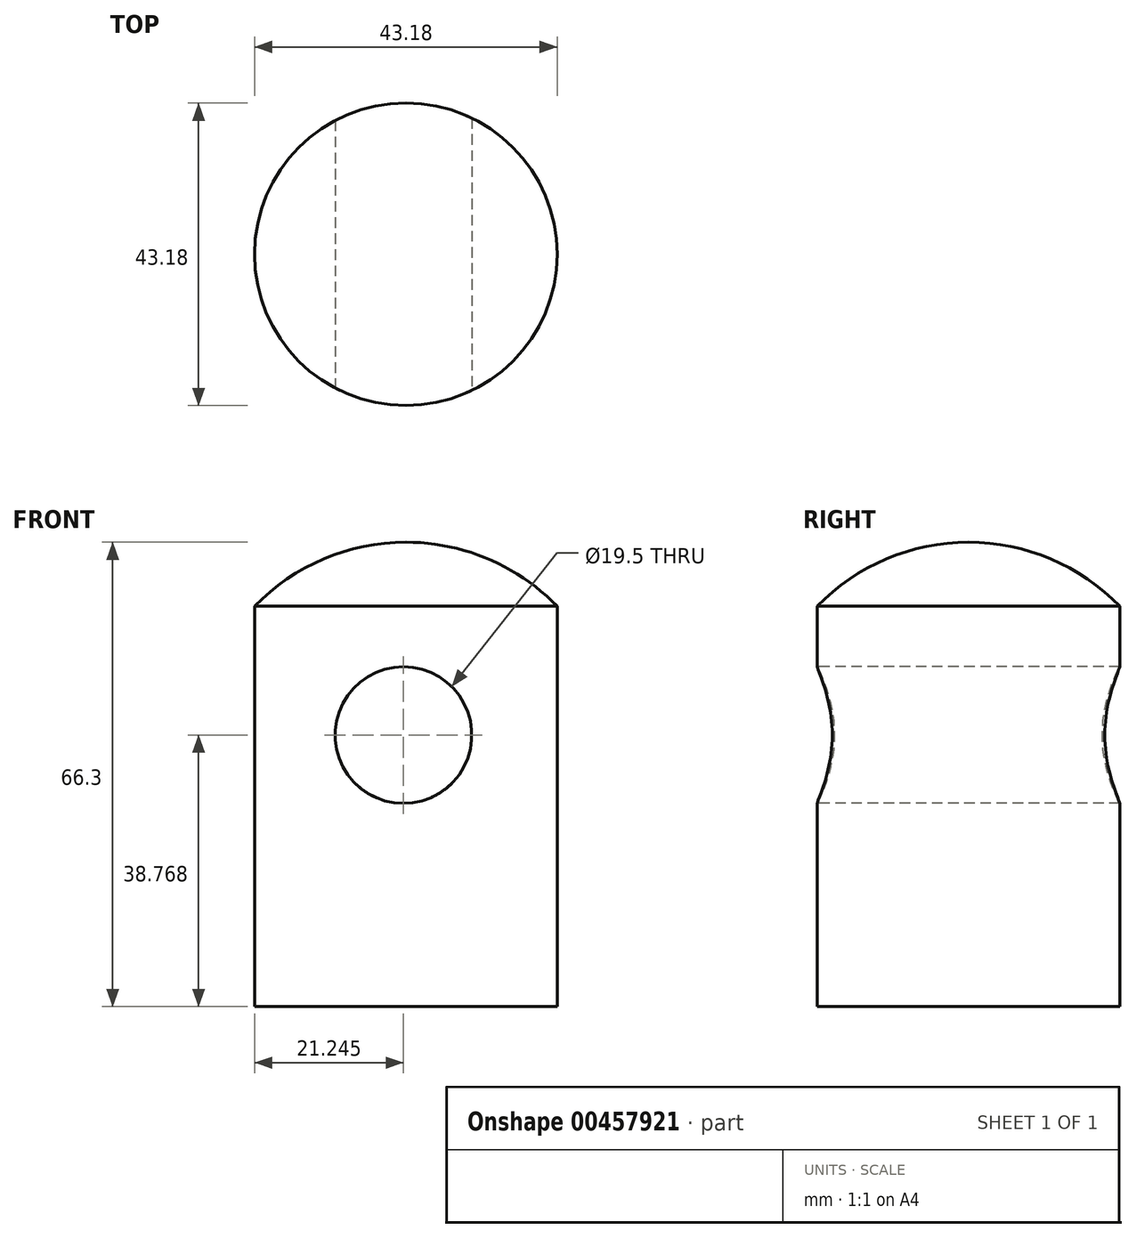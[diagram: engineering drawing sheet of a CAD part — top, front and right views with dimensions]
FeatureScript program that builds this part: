
annotation { "Feature Type Name" : "Feature", "Feature Type Description" : "" }
export const myFeature = defineFeature(function(context is Context, id is Id, definition is map)
    precondition{}
    {
        {
            var Q0;
            Q0=qCreatedBy(makeId("Front.planeOp"),FACE);
            var sketch = newSketch(context, id + "F0", { "sketchPlane" : qUnion([Q0])});
            skLineSegment(sketch, "E0.top", {"start": v(-10.6, -23.49) * mm, "end": v(11, -23.49) * mm});
            skLineSegment(sketch, "E0.left", {"start": v(-10.6, 33.66) * mm, "end": v(-10.6, -23.49) * mm});
            skLineSegment(sketch, "E0.right", {"start": v(11, 42.8) * mm, "end": v(11, -23.49) * mm});
            skArc(sketch, "E1", {"start": v(-10.6, 33.66) * mm, "mid": v(-0.73, 40.43) * mm, "end": v(11, 42.8) * mm});
            skPoint(sketch, "E2.orphan", {"position": v(32.59, 33.66) * mm});
            skSolve(sketch);
        }
        {
            var Q0;
            Q0 = qSketchRegion(id + "F0", true);
            var Q1;
            Q1=sQuery(id+"F0.wireOp",EDGE,"E0.right");
            revolve(context, id + "F1", {"entities" : qUnion([Q0]), "axis" : qUnion([Q1]), "revolveType" : RevolveType.FULL});
        }
        {
            var Q0;
            Q0=qCreatedBy(makeId("Front.planeOp"),FACE);
            var sketch = newSketch(context, id + "F2", { "sketchPlane" : qUnion([Q0])});
            skCircle(sketch, "E3", {"center": v(10.65, 15.28) * mm, "radius": 9.75 * mm});
            skSolve(sketch);
        }
        {
            var Q0;
            Q0 = qSketchRegion(id + "F2", true);
            extrude(context, id + "F3", {"entities" : qUnion([Q0]), "operationType" : NewBodyOperationType.REMOVE, "endBound" : BoundingType.THROUGH_ALL, "oppositeDirection" : true, "depth" : 25.4 * mm});
        }
        {
            var Q0;
            Q0=makeQuery(id+"F3.boolean.opBoolean","COPY",FACE,{"derivedFrom":makeQuery(id+"F3.opExtrude","CAP_FACE",FACE,{"disambiguationData":[OSD([sQuery(id+"F2.wireOp",EDGE,"E3")])],"isStart":true})});
            extrude(context, id + "F4", {"entities" : qUnion([Q0]), "operationType" : NewBodyOperationType.REMOVE, "endBound" : BoundingType.THROUGH_ALL, "oppositeDirection" : true, "depth" : 25.4 * mm});
        }
    });
